# Revit family: Lighting-Surface-Lucifer-Squilinder-SQ2-FB
name_source: partatom
category: Lighting Fixtures
revit_build: Autodesk Revit 2016 (Build: 20170117_1200(x64)
units: mm (PartAtom-declared; Revit-internal decimal feet)

## family parameters
Cut with Voids When Loaded = No
Host = Face
Light Source = Yes
Part Type = Normal
Room Calculation Point = No
Round Connector Dimension = Use Diameter
Shared = No

## types (1)
- Lighting-Surface-Lucifer-Squilinder-SQ2-FB
    Apparent Load = 0 VA
    Color Filter = 16777215
    Default Elevation = 48 "
    Description = Fixed Surface Mount
    Dimming Lamp Color Temperature Shift = <None>
    Emit Shape Visible in Rendering = Yes
    Emit from Rectangle Length = 3 "
    Emit from Rectangle Width = 3 "
    Lamp = LED
    Manufacturer = Lucifer
    Material = White Finish
    Model = SQ2-FB
    Number of Poles = 1
    Photometric Web File = Load File
    Power Factor = 1
    Tilt Angle = 90.00°
    URL = https://www.luciferlighting.com
    Voltage = 0 V

## geometry (parser evidence)
native form markers: Blend x7, Sweep x5
no freeform markers — native parametric forms only
